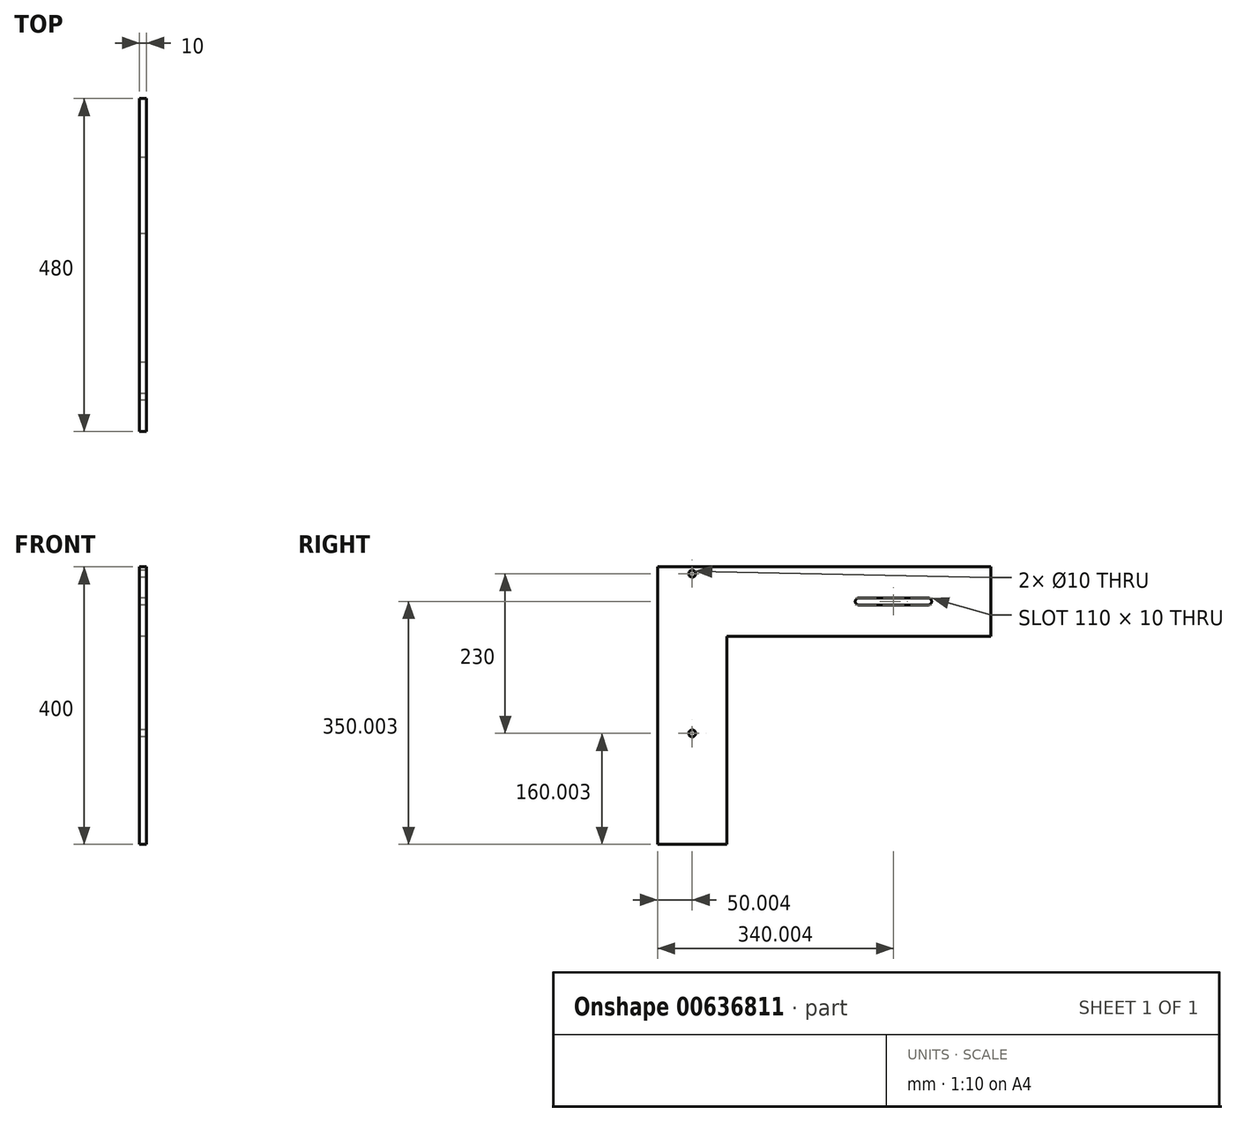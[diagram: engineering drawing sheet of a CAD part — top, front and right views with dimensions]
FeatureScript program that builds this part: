
annotation { "Feature Type Name" : "Feature", "Feature Type Description" : "" }
export const myFeature = defineFeature(function(context is Context, id is Id, definition is map)
    precondition{}
    {
        {
            var Q0;
            Q0=qCreatedBy(makeId("Right.planeOp"),FACE);
            var sketch = newSketch(context, id + "F0", { "sketchPlane" : qUnion([Q0])});
            skLineSegment(sketch, "E0.0.0", {"start": v(-217.9, -274.17) * mm, "end": v(-117.9, -274.17) * mm});
            skLineSegment(sketch, "E0.0.1", {"start": v(-117.9, -274.17) * mm, "end": v(-117.9, 25.83) * mm});
            skLineSegment(sketch, "E0.0.2", {"start": v(-117.9, 25.83) * mm, "end": v(262.1, 25.83) * mm});
            skLineSegment(sketch, "E0.0.3", {"start": v(262.1, 25.83) * mm, "end": v(262.1, 125.83) * mm});
            skLineSegment(sketch, "E0.0.4", {"start": v(262.1, 125.83) * mm, "end": v(-217.9, 125.83) * mm});
            skLineSegment(sketch, "E0.0.5", {"start": v(-217.9, 125.83) * mm, "end": v(-217.9, -274.17) * mm});
            skCircle(sketch, "E1.0", {"center": v(-167.9, 115.83) * mm, "radius": 5 * mm});
            skCircle(sketch, "E2.0", {"center": v(-167.9, -114.17) * mm, "radius": 5 * mm});
            skArc(sketch, "E3", {"start": v(172.1, 70.83) * mm, "mid": v(177.1, 75.83) * mm, "end": v(172.1, 80.83) * mm});
            skArc(sketch, "E4", {"start": v(72.1, 80.83) * mm, "mid": v(67.1, 75.83) * mm, "end": v(72.1, 70.83) * mm});
            skLineSegment(sketch, "E5", {"start": v(172.1, 80.83) * mm, "end": v(72.1, 80.83) * mm});
            skLineSegment(sketch, "E6.MirrorCS", {"start": v(172.1, 70.83) * mm, "end": v(72.1, 70.83) * mm});
            skSolve(sketch);
        }
        {
            var Q0;
            Q0=makeQuery(id+"F0.imprint","IMPRINT",FACE,{"disambiguationData":[TD([[makeQuery(id+"F0.imprint","IMPRINT",EDGE,{"derivedFrom":sQuery(id+"F0.wireOp",EDGE,"E0.0.0")}),1.0]])]});
            extrude(context, id + "F1", {"entities" : qUnion([Q0]), "depth" : 10 * mm, "offsetDistance" : 25 * mm});
        }
    });
